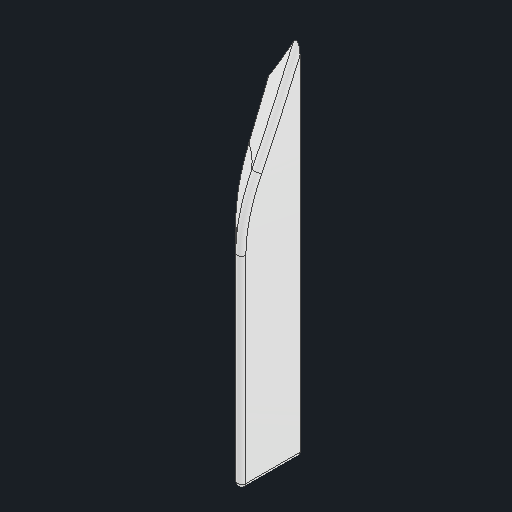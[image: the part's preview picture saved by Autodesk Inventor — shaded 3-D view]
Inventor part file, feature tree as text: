
AUTODESK INVENTOR PART (.ipt)
format: ipt  version: 2024.3 (Build 283343010, 343A)  size: 187,392 bytes
history: native  units: in
note: dims shown in document units (in); Inventor stores cm internally (conversion verified against a paired STEP export)
features: sketch x3, extrude x2, fillet x2, chamfer x1, hole x1
ambient origin geometry x8: Origin, YZ Plane, XZ Plane, XY Plane, X Axis, Y Axis, Z Axis, Center Point
bodies: Solid1 (feature_tree)
feature tree (9):
  extrude  "Extrusion1"  Depth=5.5in
  extrude  "Extrusion2"  Depth=4.5in
  chamfer  "Chamfer1"  [1 undecoded]
  fillet  "Fillet1"  Radius=3.0in
  fillet  "Fillet2"  Radius=0.75in
  sketch  "Sketch1"  dims[d3=1.0in d4=5.5in]
  sketch  "Sketch2"  dims[d5=0.5in d6=0.0in d7=4.5in d8=0.0in d9=0.0in]
  sketch  "Sketch3"  dims[d10=0.6762in d11=2.0in d12=45.0deg d13=3.0in d14=0.75in d17=0.8108in d18=0.5635in d19=0.25in d20=0.375in d21=0.235in d22=0.222in d23=0.5in d24=0.25in d25=4.0in d26=0.0625in]
  hole  "Hole1"  [1 undecoded]
note: 2 required parameter values undecoded (feature->parameter linkage not recoverable at this tier; creation-order binding heuristic only, values carry confidence <= 0.55)
